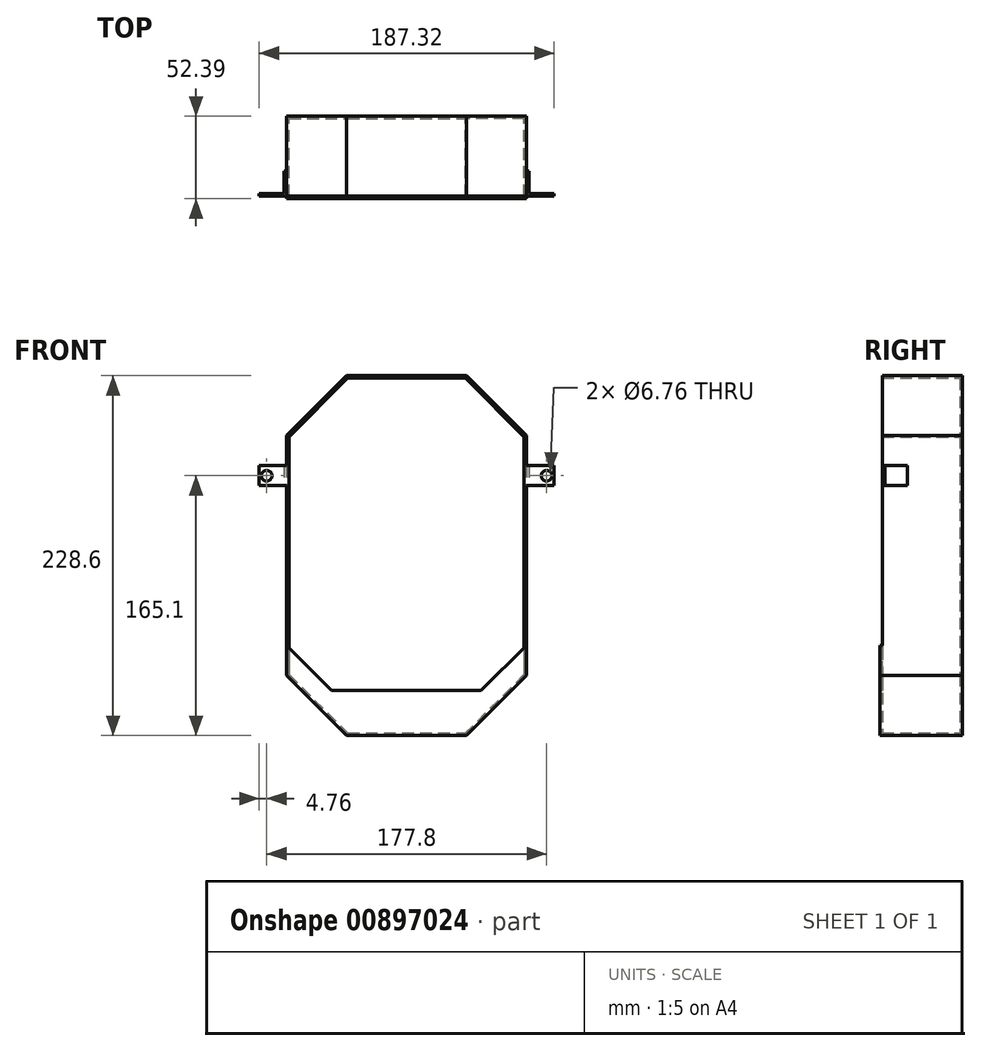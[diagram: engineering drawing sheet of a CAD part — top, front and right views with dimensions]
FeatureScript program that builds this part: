
annotation { "Feature Type Name" : "Feature", "Feature Type Description" : "" }
export const myFeature = defineFeature(function(context is Context, id is Id, definition is map)
    precondition{}
    {
        {
            var Q0;
            Q0=qCreatedBy(makeId("Front.planeOp"),FACE);
            var sketch = newSketch(context, id + "F0", { "sketchPlane" : qUnion([Q0])});
            skLineSegment(sketch, "E0", {"start": v(-76.2, 76.2) * mm, "end": v(-76.2, -76.2) * mm});
            skPoint(sketch, "E1", {"position": v(-76.2, 0) * mm});
            skLineSegment(sketch, "E2", {"start": v(-38.1, 114.3) * mm, "end": v(0, 114.3) * mm});
            skLineSegment(sketch, "E3", {"start": v(-38.1, -114.3) * mm, "end": v(0, -114.3) * mm});
            skLineSegment(sketch, "E4", {"start": v(-38.1, 114.3) * mm, "end": v(-76.2, 76.2) * mm});
            skPoint(sketch, "E5.orphan", {"position": v(-76.2, 114.3) * mm});
            skLineSegment(sketch, "E6", {"start": v(-76.2, -76.2) * mm, "end": v(-38.1, -114.3) * mm});
            skPoint(sketch, "E7.orphan", {"position": v(-76.2, -114.3) * mm});
            skLineSegment(sketch, "E8.MirrorCS", {"start": v(38.1, 114.3) * mm, "end": v(76.2, 76.2) * mm});
            skLineSegment(sketch, "E9.MirrorCS", {"start": v(38.1, -114.3) * mm, "end": v(0, -114.3) * mm});
            skLineSegment(sketch, "E10.MirrorCS", {"start": v(76.2, -76.2) * mm, "end": v(38.1, -114.3) * mm});
            skPoint(sketch, "E11.MirrorP", {"position": v(76.2, 0) * mm});
            skLineSegment(sketch, "E12.MirrorCS", {"start": v(76.2, 76.2) * mm, "end": v(76.2, -76.2) * mm});
            skLineSegment(sketch, "E13.MirrorCS", {"start": v(38.1, 114.3) * mm, "end": v(0, 114.3) * mm});
            skPoint(sketch, "E14.MirrorP", {"position": v(76.2, 114.3) * mm});
            skPoint(sketch, "E15.MirrorP", {"position": v(76.2, -114.3) * mm});
            skSolve(sketch);
        }
        {
            var Q0;
            Q0=makeQuery(id+"F0.imprint","IMPRINT",FACE,{"disambiguationData":[TD([[makeQuery(id+"F0.imprint","IMPRINT",EDGE,{"derivedFrom":sQuery(id+"F0.wireOp",EDGE,"E0")}),1.0]])]});
            extrude(context, id + "F1", {"entities" : qUnion([Q0]), "depth" : 50.8 * mm, "offsetDistance" : 25.4 * mm});
        }
        {
            var Q0;
            Q0=makeQuery(id+"F1.opExtrude","CAP_FACE",FACE,{"disambiguationData":[OSD([sQuery(id+"F0.wireOp",EDGE,"E0"),sQuery(id+"F0.wireOp",EDGE,"E2"),sQuery(id+"F0.wireOp",EDGE,"E3"),sQuery(id+"F0.wireOp",EDGE,"712c34f5-de84-4341-b5aa-e10a6b45fee00.MirrorCS"),sQuery(id+"F0.wireOp",EDGE,"712c34f5-de84-4341-b5aa-e10a6b45fee01.MirrorCS"),sQuery(id+"F0.wireOp",EDGE,"712c34f5-de84-4341-b5aa-e10a6b45fee02.MirrorCS")])],"isStart":false});
            shell(context, id + "F2", {"entities" : qUnion([Q0]), "thickness" : 1.59 * mm});
        }
        {
            var Q0;
            Q0=makeQuery(id+"F1.opExtrude","CAP_FACE",FACE,{"disambiguationData":[OSD([sQuery(id+"F0.wireOp",EDGE,"E0"),sQuery(id+"F0.wireOp",EDGE,"E2"),sQuery(id+"F0.wireOp",EDGE,"E3"),sQuery(id+"F0.wireOp",EDGE,"E4"),sQuery(id+"F0.wireOp",EDGE,"E6"),sQuery(id+"F0.wireOp",EDGE,"E8.MirrorCS"),sQuery(id+"F0.wireOp",EDGE,"E9.MirrorCS"),sQuery(id+"F0.wireOp",EDGE,"E10.MirrorCS"),sQuery(id+"F0.wireOp",EDGE,"E12.MirrorCS"),sQuery(id+"F0.wireOp",EDGE,"E13.MirrorCS")])],"isStart":false});
            var sketch = newSketch(context, id + "F3", { "sketchPlane" : qUnion([Q0])});
            skLineSegment(sketch, "E16", {"start": v(-76.2, -57.15) * mm, "end": v(-47.63, -85.73) * mm});
            skLineSegment(sketch, "E17", {"start": v(47.2, -85.73) * mm, "end": v(76.2, -57.15) * mm});
            skLineSegment(sketch, "E18", {"start": v(76.2, -57.15) * mm, "end": v(76.2, -76.2) * mm});
            skLineSegment(sketch, "E19", {"start": v(76.2, -76.2) * mm, "end": v(38.1, -114.3) * mm});
            skLineSegment(sketch, "E20", {"start": v(38.1, -114.3) * mm, "end": v(-38.1, -114.3) * mm});
            skLineSegment(sketch, "E21", {"start": v(-38.1, -114.3) * mm, "end": v(-76.2, -76.2) * mm});
            skLineSegment(sketch, "E22", {"start": v(-76.2, -76.2) * mm, "end": v(-76.2, -57.15) * mm});
            skLineSegment(sketch, "E23", {"start": v(-47.63, -85.73) * mm, "end": v(47.2, -85.73) * mm});
            skSolve(sketch);
        }
        {
            var Q0;
            Q0 = qSketchRegion(id + "F3", true);
            extrude(context, id + "F4", {"entities" : qUnion([Q0]), "operationType" : NewBodyOperationType.ADD, "depth" : 1.59 * mm, "offsetDistance" : 25.4 * mm});
        }
        {
            var Q0;
            Q0=makeQuery(id+"F4.boolean.opBoolean","MERGE",FACE,{"derivedFrom":[makeQuery(id+"F1.opExtrude","SWEPT_FACE",FACE,{"disambiguationData":[OSD([sQuery(id+"F0.wireOp",EDGE,"E0")])]}),makeQuery(id+"F4.opExtrude","SWEPT_FACE",FACE,{"disambiguationData":[OSD([sQuery(id+"F3.wireOp",EDGE,"E22")])]})]});
            var sketch = newSketch(context, id + "F5", { "sketchPlane" : qUnion([Q0])});
            skLineSegment(sketch, "E24.bottom", {"start": v(50.8, 57.15) * mm, "end": v(34.93, 57.15) * mm});
            skLineSegment(sketch, "E24.top", {"start": v(50.8, 44.45) * mm, "end": v(34.93, 44.45) * mm});
            skLineSegment(sketch, "E24.left", {"start": v(50.8, 57.15) * mm, "end": v(50.8, 44.45) * mm});
            skLineSegment(sketch, "E24.right", {"start": v(34.93, 57.15) * mm, "end": v(34.93, 44.45) * mm});
            skSolve(sketch);
        }
        {
            var Q0;
            Q0=makeQuery(id+"F5.imprint","IMPRINT",FACE,{"disambiguationData":[TD([[makeQuery(id+"F5.imprint","IMPRINT",EDGE,{"derivedFrom":sQuery(id+"F5.wireOp",EDGE,"E24.bottom")}),1.0]])]});
            extrude(context, id + "F6", {"entities" : qUnion([Q0]), "operationType" : NewBodyOperationType.ADD, "depth" : 1.59 * mm, "offsetDistance" : 25.4 * mm});
        }
        {
            var Q0;
            Q0=makeQuery(id+"F6.opExtrude","CAP_FACE",FACE,{"disambiguationData":[OSD([sQuery(id+"F5.wireOp",EDGE,"E24.bottom"),sQuery(id+"F5.wireOp",EDGE,"E24.top"),sQuery(id+"F5.wireOp",EDGE,"E24.left"),sQuery(id+"F5.wireOp",EDGE,"E24.right")])],"isStart":false});
            var sketch = newSketch(context, id + "F7", { "sketchPlane" : qUnion([Q0])});
            skLineSegment(sketch, "E25.bottom", {"start": v(50.8, 57.15) * mm, "end": v(49.21, 57.15) * mm});
            skLineSegment(sketch, "E25.top", {"start": v(50.8, 44.45) * mm, "end": v(49.21, 44.45) * mm});
            skLineSegment(sketch, "E25.left", {"start": v(50.8, 57.15) * mm, "end": v(50.8, 44.45) * mm});
            skLineSegment(sketch, "E25.right", {"start": v(49.21, 57.15) * mm, "end": v(49.21, 44.45) * mm});
            skSolve(sketch);
        }
        {
            var Q0;
            Q0=makeQuery(id+"F7.imprint","IMPRINT",FACE,{"disambiguationData":[TD([[makeQuery(id+"F7.imprint","IMPRINT",EDGE,{"derivedFrom":sQuery(id+"F7.wireOp",EDGE,"E25.bottom")}),1.0]])]});
            extrude(context, id + "F8", {"entities" : qUnion([Q0]), "operationType" : NewBodyOperationType.ADD, "depth" : 15.88 * mm, "offsetDistance" : 25.4 * mm});
        }
        {
            var Q0;
            Q0=makeQuery(id+"F8.opExtrude","SWEPT_FACE",FACE,{"disambiguationData":[OSD([sQuery(id+"F7.wireOp",EDGE,"E25.right")])]});
            var sketch = newSketch(context, id + "F9", { "sketchPlane" : qUnion([Q0])});
            skPoint(sketch, "E26.centerSnap0", {"position": v(93.66, 50.8) * mm});
            skPoint(sketch, "E27", {"position": v(88.9, 50.8) * mm});
            skSolve(sketch);
        }
        {
            var Q0;
            Q0=sQuery(id+"F9.wireOp",VERTEX,"E27");
            var Q1;
            Q1=makeQuery(id+"F1.opExtrude","SWEPT_BODY",BODY,{"disambiguationData":[OSD([sQuery(id+"F0.wireOp",EDGE,"E0"),sQuery(id+"F0.wireOp",EDGE,"E2"),sQuery(id+"F0.wireOp",EDGE,"E3"),sQuery(id+"F0.wireOp",EDGE,"E4"),sQuery(id+"F0.wireOp",EDGE,"E6"),sQuery(id+"F0.wireOp",EDGE,"E8.MirrorCS"),sQuery(id+"F0.wireOp",EDGE,"E9.MirrorCS"),sQuery(id+"F0.wireOp",EDGE,"E10.MirrorCS"),sQuery(id+"F0.wireOp",EDGE,"E12.MirrorCS"),sQuery(id+"F0.wireOp",EDGE,"E13.MirrorCS")])]});
            hole(context, id + "F10", {"style" : HoleStyle.SIMPLE, "endStyle" : HoleEndStyle.THROUGH, "standardTappedOrClearance" : lookupTablePath({ "fit" : "Free", "standard" : "ANSI", "size" : "1/4", "type" : "Clearance" }), "standardBlindInLast" : lookupTablePath({ "fit" : "Free", "standard" : "ANSI", "engagement" : "75%", "pitch" : "20 tpi", "size" : "1/4", "type" : "Clearance & tapped" }), "holeDiameter" : 6.76 * mm, "majorDiameter" : 6.35 * mm, "isTappedThrough" : true, "tappedDepth" : 19.05 * mm, "tapClearance" : 2, "startFromSketch" : true, "locations" : qUnion([Q0]), "scope" : qUnion([Q1])});
        }
        {
            var Q0;
            Q0=makeQuery(id+"F4.boolean.opBoolean","MERGE",FACE,{"derivedFrom":[makeQuery(id+"F1.opExtrude","SWEPT_FACE",FACE,{"disambiguationData":[OSD([sQuery(id+"F0.wireOp",EDGE,"E12.MirrorCS")])]}),makeQuery(id+"F4.opExtrude","SWEPT_FACE",FACE,{"disambiguationData":[OSD([sQuery(id+"F3.wireOp",EDGE,"E18")])]})]});
            var sketch = newSketch(context, id + "F11", { "sketchPlane" : qUnion([Q0])});
            skLineSegment(sketch, "E28.bottom", {"start": v(-50.8, 57.15) * mm, "end": v(-34.93, 57.15) * mm});
            skLineSegment(sketch, "E28.top", {"start": v(-50.8, 44.45) * mm, "end": v(-34.93, 44.45) * mm});
            skLineSegment(sketch, "E28.left", {"start": v(-50.8, 57.15) * mm, "end": v(-50.8, 44.45) * mm});
            skLineSegment(sketch, "E28.right", {"start": v(-34.93, 57.15) * mm, "end": v(-34.93, 44.45) * mm});
            skSolve(sketch);
        }
        {
            var Q0;
            Q0 = qSketchRegion(id + "F11", true);
            extrude(context, id + "F12", {"entities" : qUnion([Q0]), "operationType" : NewBodyOperationType.ADD, "depth" : 1.59 * mm, "offsetDistance" : 25.4 * mm});
        }
        {
            var Q0;
            Q0=makeQuery(id+"F12.opExtrude","CAP_FACE",FACE,{"disambiguationData":[OSD([sQuery(id+"F11.wireOp",EDGE,"E28.bottom"),sQuery(id+"F11.wireOp",EDGE,"E28.top"),sQuery(id+"F11.wireOp",EDGE,"E28.left"),sQuery(id+"F11.wireOp",EDGE,"E28.right")])],"isStart":false});
            var sketch = newSketch(context, id + "F13", { "sketchPlane" : qUnion([Q0])});
            skLineSegment(sketch, "E29.bottom", {"start": v(-50.8, 57.15) * mm, "end": v(-49.21, 57.15) * mm});
            skLineSegment(sketch, "E29.top", {"start": v(-50.8, 44.45) * mm, "end": v(-49.21, 44.45) * mm});
            skLineSegment(sketch, "E29.left", {"start": v(-50.8, 57.15) * mm, "end": v(-50.8, 44.45) * mm});
            skLineSegment(sketch, "E29.right", {"start": v(-49.21, 57.15) * mm, "end": v(-49.21, 44.45) * mm});
            skSolve(sketch);
        }
        {
            var Q0;
            Q0 = qSketchRegion(id + "F13", true);
            extrude(context, id + "F14", {"entities" : qUnion([Q0]), "operationType" : NewBodyOperationType.ADD, "depth" : 15.88 * mm, "offsetDistance" : 25.4 * mm});
        }
        {
            var Q0;
            Q0=makeQuery(id+"F14.opExtrude","SWEPT_FACE",FACE,{"disambiguationData":[OSD([sQuery(id+"F13.wireOp",EDGE,"E29.right")])]});
            var sketch = newSketch(context, id + "F15", { "sketchPlane" : qUnion([Q0])});
            skPoint(sketch, "E30", {"position": v(-88.9, 50.8) * mm});
            skPoint(sketch, "E30.positionSnap0", {"position": v(-93.66, 50.8) * mm});
            skSolve(sketch);
        }
        {
            var Q0;
            Q0=sQuery(id+"F15.wireOp",VERTEX,"E30");
            var Q1;
            Q1=makeQuery(id+"F1.opExtrude","SWEPT_BODY",BODY,{"disambiguationData":[OSD([sQuery(id+"F0.wireOp",EDGE,"E0"),sQuery(id+"F0.wireOp",EDGE,"E2"),sQuery(id+"F0.wireOp",EDGE,"E3"),sQuery(id+"F0.wireOp",EDGE,"E4"),sQuery(id+"F0.wireOp",EDGE,"E6"),sQuery(id+"F0.wireOp",EDGE,"E8.MirrorCS"),sQuery(id+"F0.wireOp",EDGE,"E9.MirrorCS"),sQuery(id+"F0.wireOp",EDGE,"E10.MirrorCS"),sQuery(id+"F0.wireOp",EDGE,"E12.MirrorCS"),sQuery(id+"F0.wireOp",EDGE,"E13.MirrorCS")])]});
            hole(context, id + "F16", {"style" : HoleStyle.SIMPLE, "endStyle" : HoleEndStyle.THROUGH, "standardTappedOrClearance" : lookupTablePath({ "fit" : "Free", "standard" : "ANSI", "size" : "1/4", "type" : "Clearance" }), "standardBlindInLast" : lookupTablePath({ "fit" : "Free", "standard" : "ANSI", "engagement" : "75%", "pitch" : "20 tpi", "size" : "1/4", "type" : "Clearance & tapped" }), "holeDiameter" : 6.76 * mm, "majorDiameter" : 6.35 * mm, "isTappedThrough" : true, "tappedDepth" : 19.05 * mm, "tapClearance" : 2, "startFromSketch" : true, "locations" : qUnion([Q0]), "scope" : qUnion([Q1])});
        }
    });
